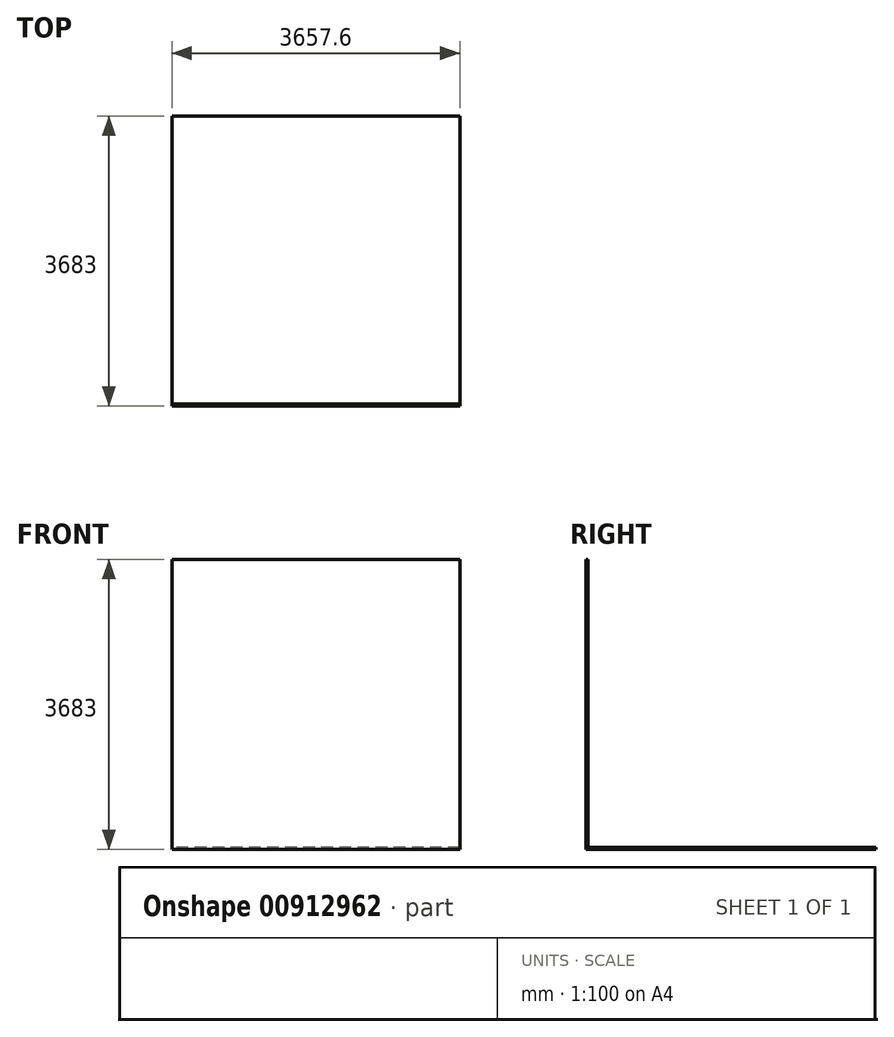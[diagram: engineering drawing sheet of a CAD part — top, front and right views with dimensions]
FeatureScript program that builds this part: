
annotation { "Feature Type Name" : "Feature", "Feature Type Description" : "" }
export const myFeature = defineFeature(function(context is Context, id is Id, definition is map)
    precondition{}
    {
        {
            var Q0;
            Q0=qCreatedBy(makeId("Right.planeOp"), FACE);
            var sketch = newSketch(context, id + "F0", { "sketchPlane" : qUnion([Q0])});
            skLineSegment(sketch, "E0", {"start": v(0, 0) * mm, "end": v(0, 3683) * mm});
            skLineSegment(sketch, "E1", {"start": v(0, 3683) * mm, "end": v(25.4, 3683) * mm});
            skLineSegment(sketch, "E2", {"start": v(25.4, 3683) * mm, "end": v(25.4, 25.4) * mm});
            skLineSegment(sketch, "E3", {"start": v(25.4, 25.4) * mm, "end": v(3683, 25.4) * mm});
            skLineSegment(sketch, "E4", {"start": v(3683, 25.4) * mm, "end": v(3683, 0) * mm});
            skLineSegment(sketch, "E5", {"start": v(3683, 0) * mm, "end": v(0, 0) * mm});
            skSolve(sketch);
        }
        {
            var Q0;
            Q0 = qSketchRegion(id + "F0", true);
            extrude(context, id + "F1", {"entities" : qUnion([Q0]), "depth" : 3657.6 * mm, "offsetDistance" : 25 * mm});
        }
    });
